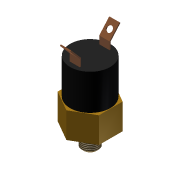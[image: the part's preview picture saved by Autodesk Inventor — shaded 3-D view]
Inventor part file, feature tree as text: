
AUTODESK INVENTOR PART (.ipt)
format: ipt  version: 2011 (Build 150239000, 239)  size: 152,064 bytes
history: native  units: mm (DEFAULTED — no unit token found)
features: extrude x6, sketch x6, projected_geometry x4, mirror x1, thread x1, chamfer x1, fillet x1
ambient origin geometry x8: Origin, YZ Plane, XZ Plane, XY Plane, X Axis, Y Axis, Z Axis, Center Point
bodies: Solid1 (feature_tree)
feature tree (20):
  extrude  "Extrusion1"  Depth=15.875mm TaperAngle=0.0deg
  extrude  "Extrusion2"  Depth=11.049mm TaperAngle=0.0deg
  extrude  "Extrusion3"  Depth=19.9898mm TaperAngle=0.0deg
  extrude  "Extrusion4"  Depth=21.971mm TaperAngle=0.0deg
  extrude  "Extrusion5"  Depth=0.762mm
  extrude  "Extrusion6"  Depth=4.699mm
  mirror  "Mirror1"
  thread  "Thread1"  [1 undecoded]
  chamfer  "Chamfer1"  Distance=6.35mm
  fillet  "Fillet1"  Radius=6.35mm
  sketch  "Sketch1"  dims[d0=25.4mm d1=15.875mm d2=0.0mm]
  sketch  "Sketch2"  dims[d3=10.16mm d4=11.049mm d5=0.0mm]
  projected_geometry  "Projected Loop1"
  sketch  "Sketch3"  dims[d6=3.175mm d7=19.9898mm d8=0.0mm]
  sketch  "Sketch4"  dims[d9=24.765mm d10=21.971mm d11=0.0mm]
  projected_geometry  "Projected Loop2"
  sketch  "Sketch5"  dims[d12=19.05mm d13=0.762mm]
  projected_geometry  "Projected Loop3"
  sketch  "Sketch6"  dims[d14=0.762mm d15=4.699mm d17=9.398mm d18=6.35mm d19=0.0mm d20=6.35mm d21=0.0mm d22=25.4mm d23=0.0mm d24=1.0mm d25=3.175mm d26=45.0deg d27=3.175mm]
  projected_geometry  "Projected Loop4"
note: 1 required parameter value undecoded (feature->parameter linkage not recoverable at this tier; creation-order binding heuristic only, values carry confidence <= 0.55)
